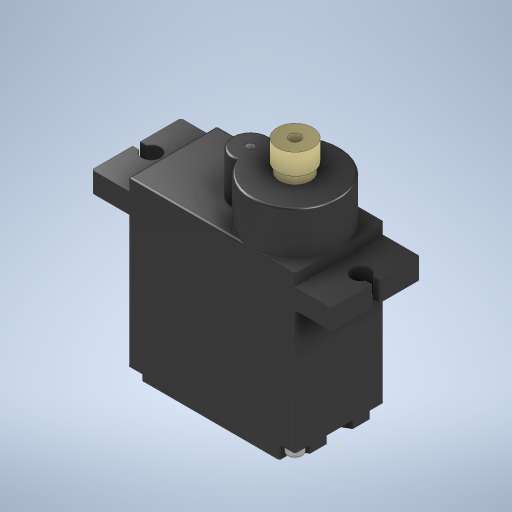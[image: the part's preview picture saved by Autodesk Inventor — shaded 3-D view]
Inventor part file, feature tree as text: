
AUTODESK INVENTOR PART (.ipt)
format: ipt  version: 2023 (Build 270158000, 158)  size: 588,800 bytes
history: native  units: mm
features: extrude x16, sketch x12, fillet x4, other x2, projected_geometry x2
ambient origin geometry x8: Origin, YZ Plane, XZ Plane, XY Plane, X Axis, Y Axis, Z Axis, Center Point
bodies: Body1 (feature_tree)
feature tree (36):
  other  "솔리드1"
  extrude  "돌출1"  Depth=22.5mm
  other  "작업 평면1"
  extrude  "돌출2"  Depth=12.0mm
  extrude  "돌출3"  Depth=23.0mm TaperAngle=0.0deg
  sketch  "스케치4"
  extrude  "돌출6"  [1 undecoded]
  extrude  "돌출7"  Depth=32.2mm
  fillet  "모깎기1"  Radius=12.0mm
  fillet  "모깎기2"  Radius=2.5mm
  sketch  "스케치5"
  extrude  "돌출8"  Depth=2.0mm
  extrude  "돌출9"  Depth=0.5mm
  extrude  "돌출10"  Depth=0.5mm
  extrude  "돌출11"  Depth=2.7mm TaperAngle=0.0deg
  fillet  "모깎기3"  Radius=1.0mm
  sketch  "스케치7"
  extrude  "돌출12"  Depth=1.5mm TaperAngle=0.0deg
  extrude  "돌출13"  Depth=5.0mm
  extrude  "돌출14"  Depth=6.0mm
  extrude  "돌출15"  Depth=5.0mm
  fillet  "모깎기4"  Radius=1.0mm
  extrude  "돌출16"  Depth=5.8mm TaperAngle=0.0deg
  sketch  "스케치12"
  sketch  "스케치14"
  extrude  "돌출18"  Depth=5.01mm TaperAngle=0.0deg
  extrude  "돌출19"  Depth=0.3mm
  sketch  "스케치15"
  sketch  "스케치16"
  sketch  "스케치17"
  sketch  "스케치1"
  sketch  "스케치2"
  sketch  "스케치3"
  projected_geometry  "투영된 루프1"
  projected_geometry  "투영된 루프2"
  sketch  "스케치6"
note: 1 required parameter value undecoded (feature->parameter linkage not recoverable at this tier; creation-order binding heuristic only, values carry confidence <= 0.55)
